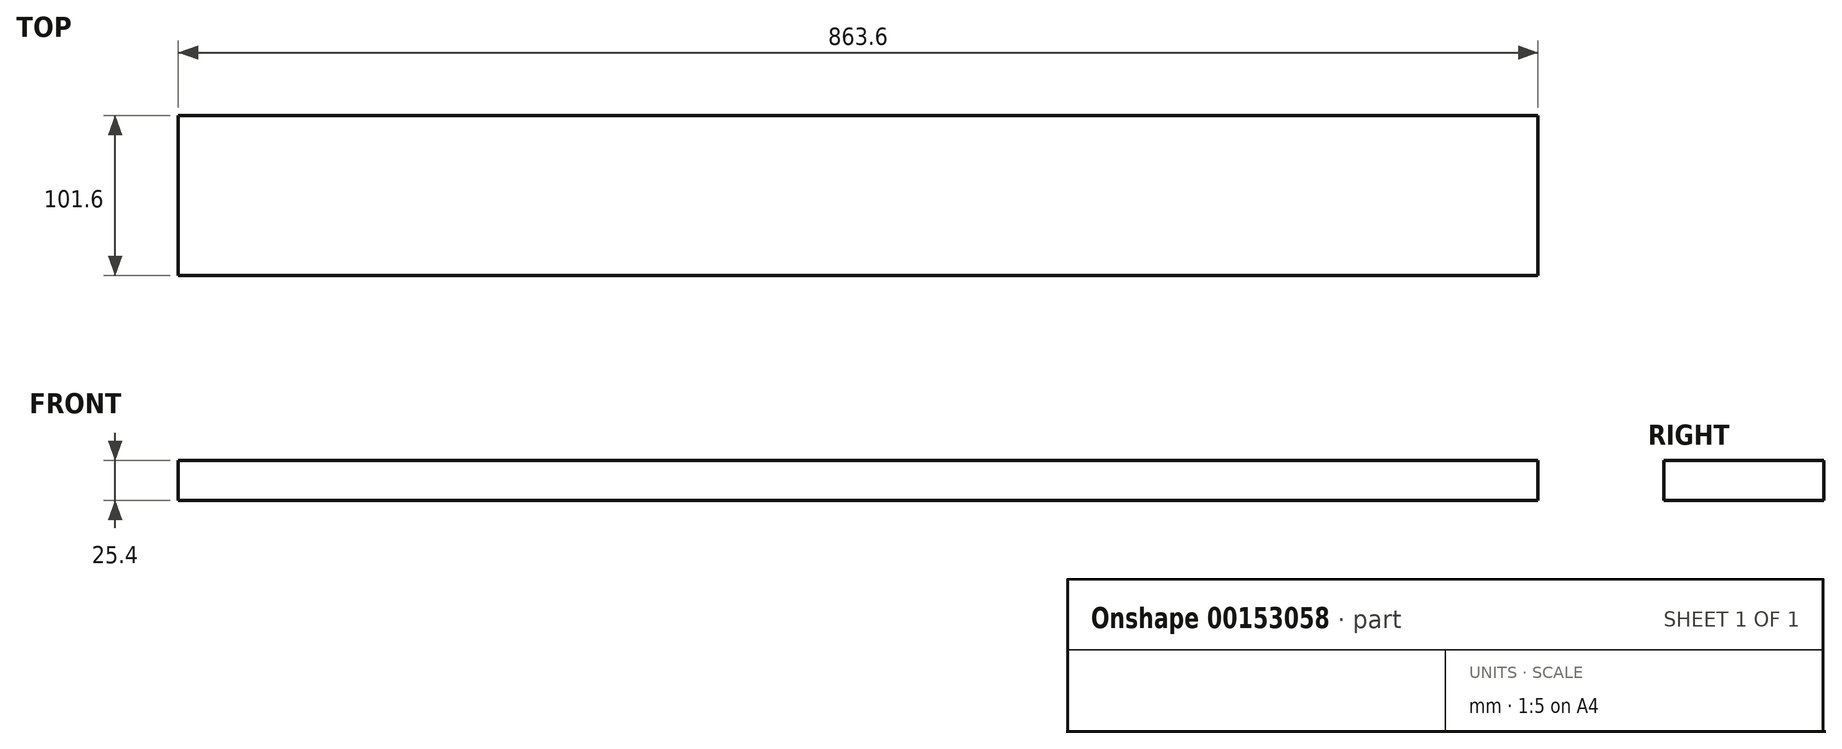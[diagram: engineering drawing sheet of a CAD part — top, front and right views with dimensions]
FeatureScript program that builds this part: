
annotation { "Feature Type Name" : "Feature", "Feature Type Description" : "" }
export const myFeature = defineFeature(function(context is Context, id is Id, definition is map)
    precondition{}
    {
        {
            var Q0;
            Q0=qCreatedBy(makeId("Top.planeOp"),FACE);
            var sketch = newSketch(context, id + "F0", { "sketchPlane" : qUnion([Q0])});
            skLineSegment(sketch, "E0.bottom", {"start": v(0, 0) * mm, "end": v(863.6, 0) * mm});
            skLineSegment(sketch, "E0.top", {"start": v(0, 101.6) * mm, "end": v(863.6, 101.6) * mm});
            skLineSegment(sketch, "E0.left", {"start": v(0, 0) * mm, "end": v(0, 101.6) * mm});
            skLineSegment(sketch, "E0.right", {"start": v(863.6, 0) * mm, "end": v(863.6, 101.6) * mm});
            skSolve(sketch);
        }
        {
            var Q0;
            Q0=makeQuery(id+"F0.imprint","IMPRINT",FACE,{"disambiguationData":[TD([[makeQuery(id+"F0.imprint","IMPRINT",EDGE,{"derivedFrom":sQuery(id+"F0.wireOp",EDGE,"E0.bottom")}),1.0]])]});
            extrude(context, id + "F1", {"entities" : qUnion([Q0]), "depth" : 25.4 * mm});
        }
    });
